# Revit family: OHM-NRG
name_source: partatom
category: Mechanical Equipment
units: mm (PartAtom-declared; Revit-internal decimal feet)

## family parameters
Always vertical = Yes
Cut with Voids When Loaded = No
OmniClass Number = 23.40.40.11.17
OmniClass Title = Refrigerated Cases
Part Type = Normal
Room Calculation Point = No
Round Connector Dimension = Use Radius
Shared = No
Work Plane-Based = Yes

## types (12) — shared parameters
16" Shelf = Yes
18" Shelf = Yes
20" Shelf = Yes
30" x 64" 1 Door = Yes
BOTTOM ELECTRICAL = Yes
BOTTOM REFRIGERATION PIPING = Yes
Certifications = NSF 7, UL471, CSA
DATE = 05/02/2016
DRAIN PIPING = Yes
Default Elevation = 48"
Defrosts Per Day = 6
Description = Multi-Deck Merchandiser
Discharge Air (°F) = 30 °F
Discharge Air Velocity (FPM) = 200 FPM
EQUIPMENT DESCRIPTION = Multi-Deck Merchandiser
EQUIPMENT MARK = OHM-NRG-5BF
Electric Defrost Fail-Safe = 35 (Min)
Electric Defrost Termination Temp (°F) = 47 °F
Evaporator (°F) = 27 °F
GLASS = Glass
Height = 69 1/2"
Hot Gas Defrost Fail-Safe = 26 (Min)
Hot Gas Defrost Termination Temp (°F) = 45 °F
Item Description = Multi-Deck Merchandiser
LF STD END = Yes
Legend Number = OHM-NRG-5BF
Manufacturer = HILL PHOENIX
Model = OHM-NRG-5BF
PAINTED METAL UPPER SHELF = PAINTED SHELVES
REAR REFRIGERATION PIPING = Yes
RT STD END = Yes
Run-Off Time (Min) = 6-8 (Min)
Standard Power Amps = 0 A
Superheat Set Point @ Bulb (°F) = 6-8 °F
TOP ELECTRICAL = Yes
TOP REFRIGERATION PIPING = Yes
Timed-Off Defrost Fail-Safe (Min) = 40 (Min)
Timed-Off Defrost Termination Temp = 42 °F
URL = http://www.hillphoenix.com
Width = 43 1/4"

## per-type parameters (varying)
| type | BTUH Conventional | BTUH Parallel | CENTER LINE | DRAIN LINE | Defrost (Phase 1) 208 V Amps | Defrost (Phase 1) 208 V Watts | Defrost (Phase 1) 240 V Amps | Defrost (Phase 1) 240 V Watts | Front/Rear Sill Heights | High Efficiency Amps | High Efficiency Watts | High Power (Cornice) Amps | High Power (Cornice) Watts | Length | Length of Cases | Light Length | Lights Per Row | Number of Fans | Refgn | Standard Power Watts |
| 04' Standard Sill Height | 1371 | 1200 | 24" | 36" | 2 A | 400 W | 2 A | 532 W | Standard | 0 A | 23 W | 0 A | 22 W | 48" | 48" | 4' | 1 | 2 | 22 1/2" | 12 W |
| 06' Standard Sill Height | 1371 | 1200 | 36" | 36" | 3 A | 600 W | 3 A | 798 W | Standard | 0 A | 23 W | 0 A | 30 W | 72" | 72" | 3' | 2 | 2 | 28 5/8" | 17 W |
| 08' Standard Sill Height | 1410 | 1273 | 48" | 48" | 4 A | 800 W | 4 A | 1065 W | Standard | 1 A | 35 W | 0 A | 43 W | 96" | 96" | 3' | 2 | 3 | 28 5/8" | 24 W |
| 12' Standard Sill Height | 1410 | 1273 | 72" | 72" | 6 A | 1200 W | 7 A | 1600 W | Standard | 1 A | 47 W | 1 A | 65 W | 144" | 144" | 4' | 3 | 4 | 28 5/8" | 36 W |
| 04' All Other Sill Heights | 1250 | 1094 | 24" | 36" | 2 A | 400 W | 2 A | 532 W | All Others | 0 A | 23 W | 0 A | 22 W | 48" | 48" | 4' | 1 | 2 | 22 1/2" | 12 W |
| 06' All Other Sill Heights | 1250 | 1094 | 36" | 36" | 3 A | 600 W | 3 A | 798 W | All Others | 0 A | 23 W | 0 A | 30 W | 72" | 72" | 3' | 2 | 2 | 28 5/8" | 17 W |
| 08' All Other Sill Heights | 1361 | 1229 | 48" | 48" | 4 A | 800 W | 4 A | 1065 W | All Others | 1 A | 35 W | 0 A | 43 W | 96" | 96" | 3' | 2 | 3 | 28 5/8" | 24 W |
| 12' All Other Sill Heights | 1361 | 1229 | 72" | 72" | 6 A | 1200 W | 7 A | 1600 W | All Others | 1 A | 47 W | 1 A | 65 W | 144" | 144" | 4' | 3 | 4 | 28 5/8" | 36 W |
| 12' | 1371 | 1200 | 72" | 72" | 6 A | 1200 W | 7 A | 1600 W | Standard | 1 A | 72 W | 0 A | 45 W | 144" | 144" | 4' | 3 | 4 | 28 5/8" | 18 W |
| 8' | 1371 | 1200 | 48" | 48" | 4 A | 800 W | 4 A | 1065 W | Standard | 1 A | 54 W | 0 A | 30 W | 96" | 96" | 4' | 2 | 3 | 28 5/8" | 12 W |
| 6' | 1250 | 1094 | 36" | 36" | 3 A | 600 W | 3 A | 798 W | All Others | 1 A | 54 W | 0 A | 24 W | 72" | 72" | 3' | 2 | 3 | 28 5/8" | 9 W |
| 4' | 1371 | 1200 | 24" | 36" | 2 A | 400 W | 2 A | 532 W | Standard | 1 A | 36 W | 0 A | 15 W | 48" | 48" | 4' | 1 | 2 | 22 1/2" | 6 W |

## geometry (parser evidence)
native form markers: Blend x17, Sweep x15
no freeform markers — native parametric forms only
